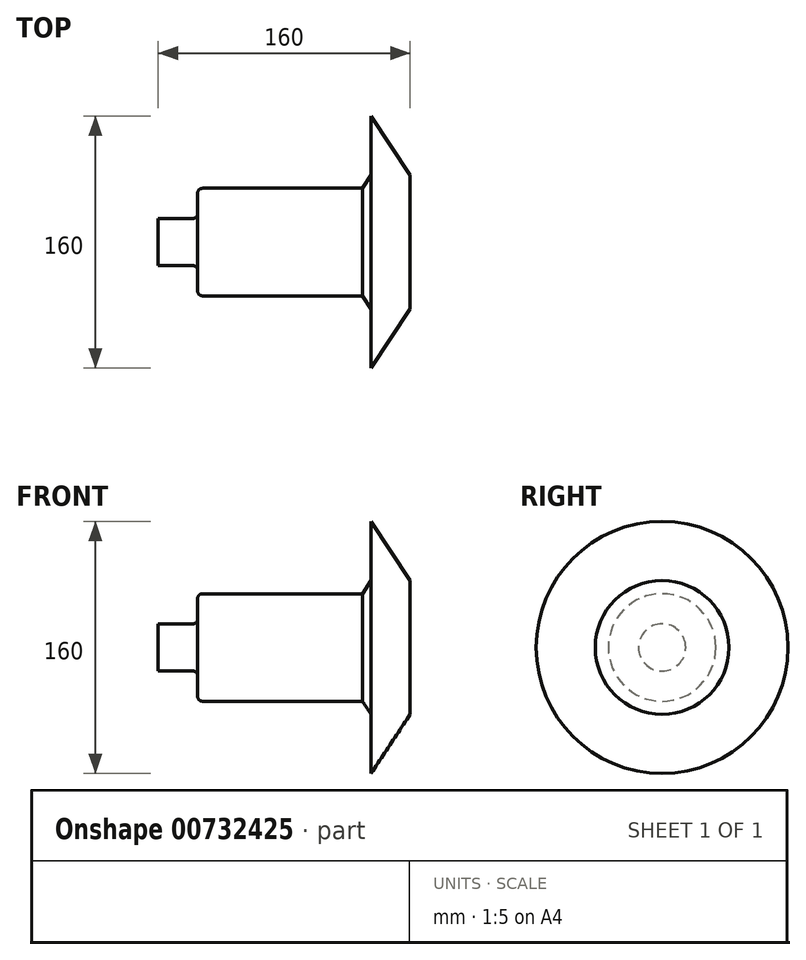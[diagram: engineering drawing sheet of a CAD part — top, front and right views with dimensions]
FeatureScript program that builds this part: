
annotation { "Feature Type Name" : "Feature", "Feature Type Description" : "" }
export const myFeature = defineFeature(function(context is Context, id is Id, definition is map)
    precondition{}
    {
        {
            var Q0;
            Q0=qCreatedBy(makeId("Front.planeOp"),FACE);
            var sketch = newSketch(context, id + "F0", { "sketchPlane" : qUnion([Q0])});
            skLineSegment(sketch, "E0", {"start": v(-160, 0) * mm, "end": v(-160, 15) * mm});
            skLineSegment(sketch, "E1", {"start": v(-160, 15) * mm, "end": v(-135, 15) * mm});
            skLineSegment(sketch, "E2", {"start": v(-135, 15) * mm, "end": v(-135, 34.14) * mm});
            skLineSegment(sketch, "E3", {"start": v(-135, 34.14) * mm, "end": v(-30.36, 34.14) * mm});
            skLineSegment(sketch, "E4", {"start": v(-30.36, 34.14) * mm, "end": v(-24.81, 42.46) * mm});
            skLineSegment(sketch, "E5", {"start": v(-24.81, 42.46) * mm, "end": v(-24.81, 80) * mm});
            skLineSegment(sketch, "E6", {"start": v(-24.81, 80) * mm, "end": v(0, 42.46) * mm});
            skLineSegment(sketch, "E7", {"start": v(0, 42.46) * mm, "end": v(0, 0) * mm});
            skLineSegment(sketch, "E8", {"start": v(0, 0) * mm, "end": v(-160, 0) * mm});
            skSolve(sketch);
        }
        {
            var Q0;
            Q0=makeQuery(id+"F0.imprint","IMPRINT",FACE,{"disambiguationData":[TD([[makeQuery(id+"F0.imprint","IMPRINT",EDGE,{"derivedFrom":sQuery(id+"F0.wireOp",EDGE,"E0")}),-1.0]])]});
            var Q1;
            Q1=sQuery(id+"F0.wireOp",EDGE,"E8");
            revolve(context, id + "F1", {"surfaceOperationType" : NewSurfaceOperationType.NEW, "entities" : qUnion([Q0]), "axis" : qUnion([Q1]), "revolveType" : RevolveType.FULL});
        }
        {
            var Q0;
            Q0=makeQuery(id+"F1.opRevolve","SWEPT_FACE",FACE,{"disambiguationData":[OSD([sQuery(id+"F0.wireOp",EDGE,"E2")])]});
            fillet(context, id + "F2", {"entities" : qUnion([Q0]), "radius" : 3 * mm, "tangentPropagation" : true, "allowEdgeOverflow" : false});
        }
    });
